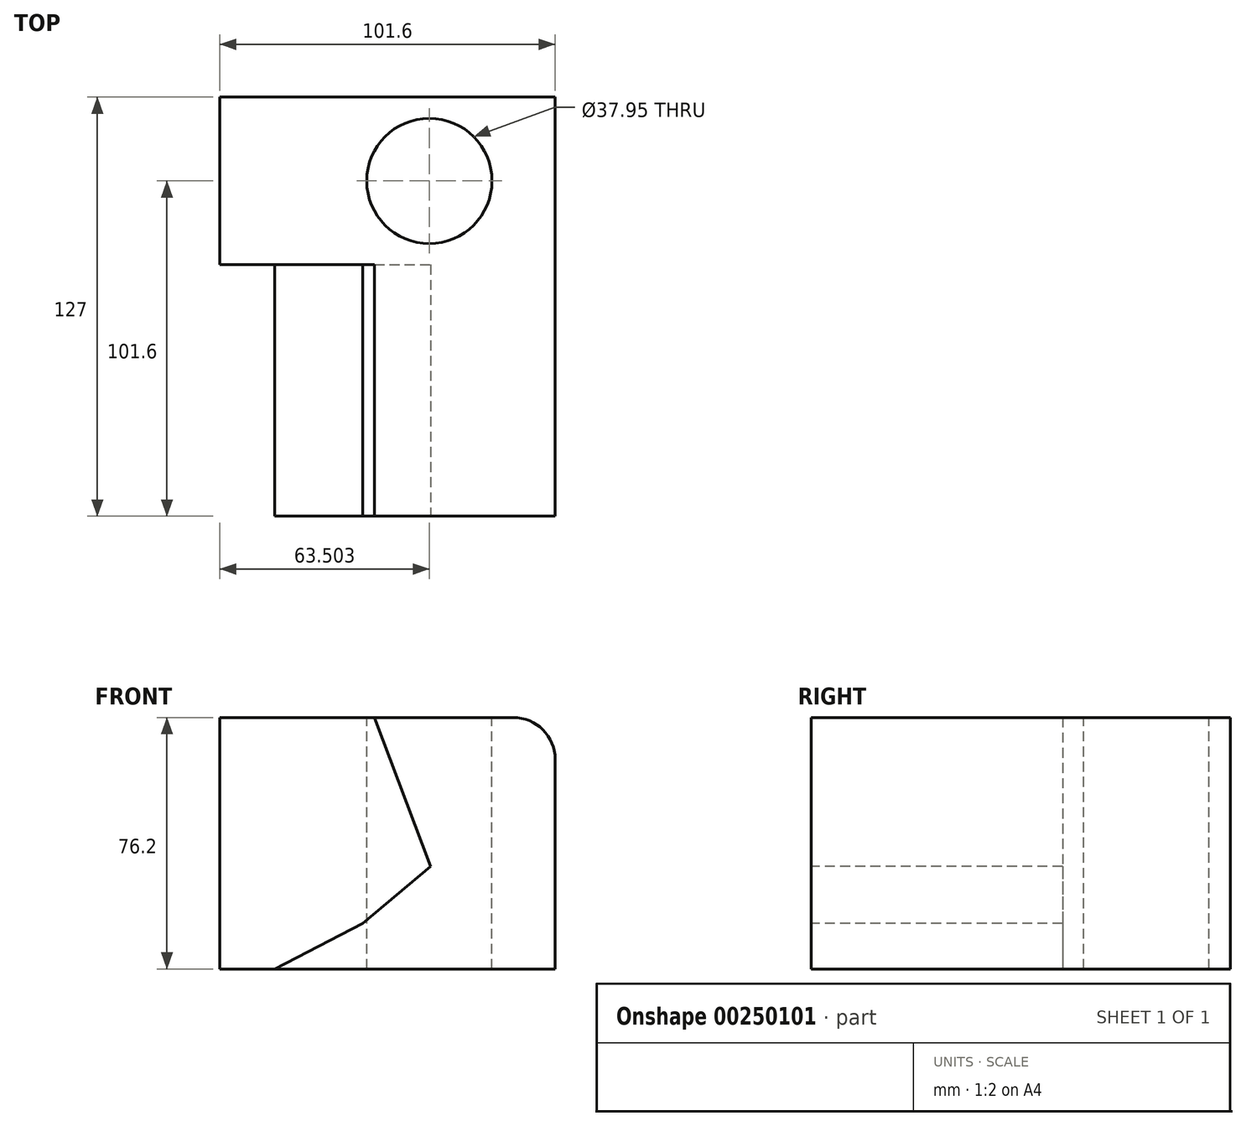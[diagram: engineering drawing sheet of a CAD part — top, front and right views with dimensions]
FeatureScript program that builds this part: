
annotation { "Feature Type Name" : "Feature", "Feature Type Description" : "" }
export const myFeature = defineFeature(function(context is Context, id is Id, definition is map)
    precondition{}
    {
        {
            var Q0;
            Q0=qCreatedBy(makeId("Front.planeOp"),FACE);
            var sketch = newSketch(context, id + "F0", { "sketchPlane" : qUnion([Q0])});
            skLineSegment(sketch, "E0.bottom", {"start": v(-34.65, 45.09) * mm, "end": v(66.95, 45.09) * mm});
            skLineSegment(sketch, "E0.top", {"start": v(-34.65, -31.11) * mm, "end": v(66.95, -31.11) * mm});
            skLineSegment(sketch, "E0.left", {"start": v(-34.65, 45.09) * mm, "end": v(-34.65, -31.11) * mm});
            skLineSegment(sketch, "E0.right", {"start": v(66.95, 45.09) * mm, "end": v(66.95, -31.11) * mm});
            skSolve(sketch);
        }
        {
            var Q0;
            Q0=makeQuery(id+"F0.imprint","IMPRINT",FACE,{"disambiguationData":[TD([[makeQuery(id+"F0.imprint","IMPRINT",EDGE,{"derivedFrom":sQuery(id+"F0.wireOp",EDGE,"E0.bottom")}),-1.0]])]});
            extrude(context, id + "F1", {"entities" : qUnion([Q0]), "depth" : 127 * mm});
        }
        {
            var Q0;
            Q0=makeQuery(id+"F1.opExtrude","CAP_FACE",FACE,{"disambiguationData":[OSD([sQuery(id+"F0.wireOp",EDGE,"E0.bottom"),sQuery(id+"F0.wireOp",EDGE,"E0.top"),sQuery(id+"F0.wireOp",EDGE,"E0.left"),sQuery(id+"F0.wireOp",EDGE,"E0.right")])],"isStart":false});
            var sketch = newSketch(context, id + "F2", { "sketchPlane" : qUnion([Q0])});
            skLineSegment(sketch, "E1", {"start": v(-34.65, 45.09) * mm, "end": v(12.22, 45.09) * mm});
            skLineSegment(sketch, "E2", {"start": v(12.22, 45.09) * mm, "end": v(29.27, 0) * mm});
            skLineSegment(sketch, "E3", {"start": v(29.27, 0) * mm, "end": v(8.6, -17.29) * mm});
            skLineSegment(sketch, "E4", {"start": v(8.6, -17.29) * mm, "end": v(-17.96, -31.11) * mm});
            skLineSegment(sketch, "E5", {"start": v(-17.96, -31.11) * mm, "end": v(-34.65, -31.11) * mm});
            skLineSegment(sketch, "E6", {"start": v(-34.65, -31.11) * mm, "end": v(-34.65, 45.09) * mm});
            skSolve(sketch);
        }
        {
            var Q0;
            Q0=makeQuery(id+"F2.imprint","IMPRINT",FACE,{"disambiguationData":[TD([[makeQuery(id+"F2.imprint","IMPRINT",EDGE,{"derivedFrom":sQuery(id+"F2.wireOp",EDGE,"E1")}),-1.0]])]});
            extrude(context, id + "F3", {"entities" : qUnion([Q0]), "operationType" : NewBodyOperationType.REMOVE, "oppositeDirection" : true, "depth" : 76.2 * mm});
        }
        {
            var Q0;
            Q0=makeQuery(id+"F1.opExtrude","SWEPT_EDGE",EDGE,{"disambiguationData":[OSD([sQuery(id+"F0.wireOp",EDGE,"E0.bottom"),sQuery(id+"F0.wireOp",EDGE,"E0.right")])]});
            fillet(context, id + "F4", {"entities" : qUnion([Q0]), "radius" : 12.7 * mm, "tangentPropagation" : true, "allowEdgeOverflow" : false});
        }
        {
            var Q0;
            Q0=makeQuery(id+"F1.opExtrude","SWEPT_FACE",FACE,{"disambiguationData":[OSD([sQuery(id+"F0.wireOp",EDGE,"E0.bottom")])]});
            var sketch = newSketch(context, id + "F5", { "sketchPlane" : qUnion([Q0])});
            skCircle(sketch, "E7", {"center": v(28.85, -25.4) * mm, "radius": 18.98 * mm});
            skSolve(sketch);
        }
        {
            var Q0;
            Q0=makeQuery(id+"F5.imprint","IMPRINT",FACE,{"disambiguationData":[TD([[makeQuery(id+"F5.imprint","IMPRINT",EDGE,{"derivedFrom":sQuery(id+"F5.wireOp",EDGE,"E7")}),1.0]])]});
            extrude(context, id + "F6", {"entities" : qUnion([Q0]), "operationType" : NewBodyOperationType.REMOVE, "oppositeDirection" : true, "depth" : 1270 * mm});
        }
    });
